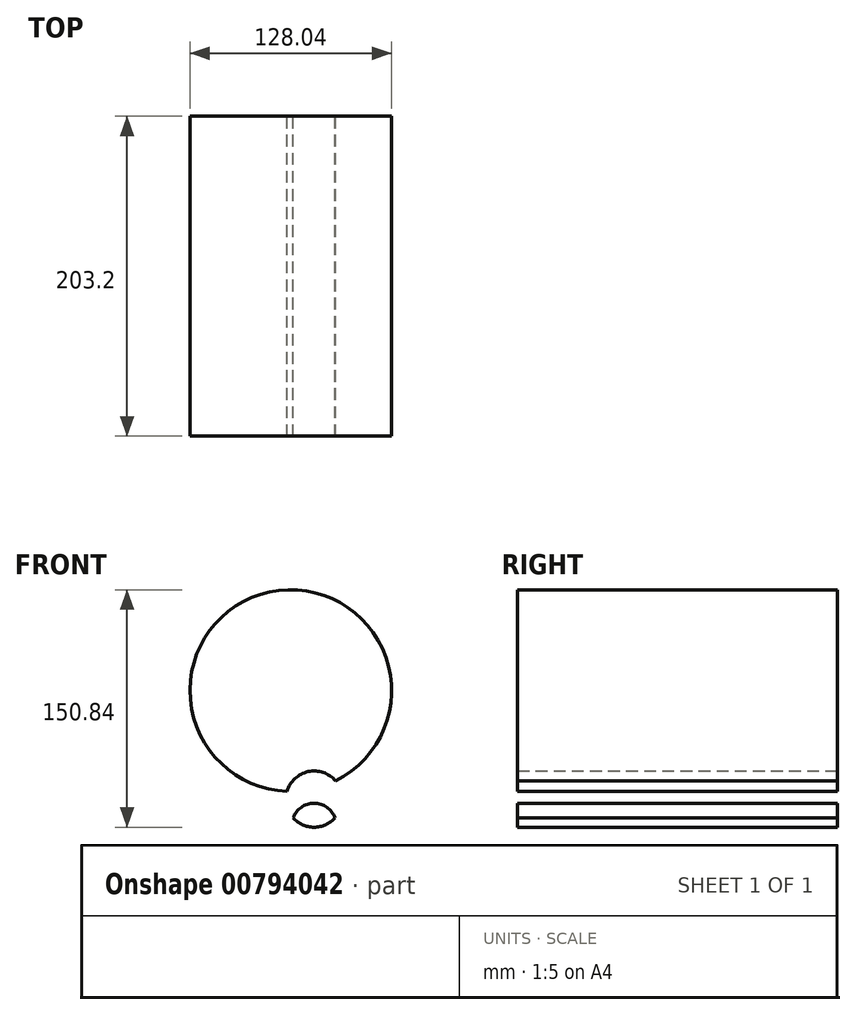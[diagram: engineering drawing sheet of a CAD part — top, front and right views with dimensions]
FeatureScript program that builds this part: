
annotation { "Feature Type Name" : "Feature", "Feature Type Description" : "" }
export const myFeature = defineFeature(function(context is Context, id is Id, definition is map)
    precondition{}
    {
        {
            var Q0;
            Q0=qCreatedBy(makeId("Front.planeOp"),FACE);
            var sketch = newSketch(context, id + "F0", { "sketchPlane" : qUnion([Q0])});
            skArc(sketch, "E0", {"start": v(-37.1, -11.4) * mm, "mid": v(-78.94, 108.57) * mm, "end": v(-67.8, -18) * mm});
            skArc(sketch, "E1", {"start": v(-64, -34.85) * mm, "mid": v(-50.67, -40.84) * mm, "end": v(-37.33, -34.85) * mm});
            skArc(sketch, "E2", {"start": v(-37.33, -34.85) * mm, "mid": v(-50.67, -25.66) * mm, "end": v(-64, -34.85) * mm});
            skArc(sketch, "E3.trimOffspring", {"start": v(-37.1, -11.4) * mm, "mid": v(-54.42, -5.54) * mm, "end": v(-67.8, -18) * mm});
            skSolve(sketch);
        }
        {
            var Q0;
            {var subQ0=sQuery(id+"F0.wireOp",EDGE,"E1");var subQ1=sQuery(id+"F0.wireOp",EDGE,"E0");var subQ2=makeQuery(id+"F0.imprint","INTERSECT",VERTEX,{"disambiguationData":[OD(0.0)],"derivedFrom":[subQ1,subQ0]});Q0=makeQuery(id+"F0.imprint","IMPRINT",FACE,{"disambiguationData":[TD([[makeQuery(id+"F0.imprint","IMPRINT",EDGE,{"disambiguationData":[TD([[subQ2,1.0]])],"derivedFrom":subQ1}),1.0]])]});}
            var Q1;
            {var subQ0=sQuery(id+"F0.wireOp",EDGE,"E2");var subQ1=sQuery(id+"F0.wireOp",EDGE,"E1");var subQ2=makeQuery(id+"F0.imprint","INTERSECT",VERTEX,{"disambiguationData":[OD(0.0)],"derivedFrom":[subQ1,subQ0]});Q1=makeQuery(id+"F0.imprint","IMPRINT",FACE,{"disambiguationData":[TD([[makeQuery(id+"F0.imprint","IMPRINT",EDGE,{"disambiguationData":[TD([[subQ2,-1.0]])],"derivedFrom":subQ1}),1.0]])]});}
            extrude(context, id + "F1", {"entities" : qUnion([Q0, Q1]), "depth" : 203.2 * mm, "offsetDistance" : 25.4 * mm});
        }
    });
